# Revit family: WALL SQUARE 6W SIMETRICA_LKB0635A_WW
name_source: partatom
category: Luminarias
units: mm (PartAtom-declared; Revit-internal decimal feet)

## family parameters
Compartido = No
Corte con vacíos al cargar = No
Cota de conector redondo = Diámetro de uso
Origen de luz = Sí
Punto de cálculo de habitación = No
Se basa en plano de trabajo = Sí
Siempre vertical = No
Tipo de pieza = Normal

## types (8) — shared parameters
Ancho = 160 mm  [stored 0.524934 ft]
Cambio de temperatura de color de luz atenuada = <Ninguno>
Comentarios de vataje = 100-240V
Fabricante = BRILLANT
Filtro de color = 16777215
Longitud de símbolo de origen de luz = 500 mm  [stored 1.64042 ft]
Lámpara = OSRAM
Watt per fixture = 6
Ángulo de inclinación = 105.00°
zero-valued in all types: Elevación por defecto

## per-type parameters (varying)
| type | Descripción | Modelo | Ángulo de campo de foco | Ángulo de enfoque |
| EMP_LKB0635A.30 | LUMINARIA TIPO CUADRADO PARA EMPOTRAR EN PISO CON CUERPO DE ALUMINIO FUNDIDO A PRESION, CUBIERTO CON POLVO GRIS OSCURO CON CUBIERTA DE ACERO INOXIDABLE Y VIDRIO TEMPLADO DE 8MM, HOUSING DE METAL 1.5MM CUBIERTO DE POLVO GRIS OSCURO DE 160MM Y 118MM DE PROFUNDO CON PESO DE 2.5KG. CUENTA CON 6 LED TIPO OSRAM CON UNA POTENCIA TOTAL DE 6W, TEMPERATURA EN BLANCO ULTRA CALIDO EN 2000K CON 269 LUMENES, IP67, IK09, IRC 80 APERTURA EN 30 GRADOS POR STOCK, ALIMENTADA A 100-240V. | LKB0635A.30 | 30.00° | 30.00° |
| EMP_LKB0635A.6 | LUMINARIA TIPO CUADRADO PARA EMPOTRAR EN PISO CON CUERPO DE ALUMINIO FUNDIDO A PRESION, CUBIERTO CON POLVO GRIS OSCURO CON CUBIERTA DE ACERO INOXIDABLE Y VIDRIO TEMPLADO DE 8MM, HOUSING DE METAL 1.5MM CUBIERTO DE POLVO GRIS OSCURO DE 160MM Y 118MM DE PROFUNDO CON PESO DE 2.5KG. CUENTA CON 6 LED TIPO OSRAM CON UNA POTENCIA TOTAL DE 6W, TEMPERATURA EN BLANCO ULTRA CALIDO EN 2000K CON 269 LUMENES, IP67, IK09, IRC 80 APERTURA EN 6 GRADOS POR PROYECTO, ALIMENTADA A 100-240V. | LKB0635A.6 | 6.00° | 6.00° |
| EMP_LKB0635A.13 | LUMINARIA TIPO CUADRADO PARA EMPOTRAR EN PISO CON CUERPO DE ALUMINIO FUNDIDO A PRESION, CUBIERTO CON POLVO GRIS OSCURO CON CUBIERTA DE ACERO INOXIDABLE Y VIDRIO TEMPLADO DE 8MM, HOUSING DE METAL 1.5MM CUBIERTO DE POLVO GRIS OSCURO DE 160MM Y 118MM DE PROFUNDO CON PESO DE 2.5KG. CUENTA CON 6 LED TIPO OSRAM CON UNA POTENCIA TOTAL DE 6W, TEMPERATURA EN BLANCO ULTRA CALIDO EN 2000K CON 269 LUMENES, IP67, IK09, IRC 80 APERTURA EN 13 GRADOS POR PROYECTO, ALIMENTADA A 100-240V. | LKB0635A.13 | 13.00° | 13.00° |
| EMP_LKB0635A.20 | LUMINARIA TIPO CUADRADO PARA EMPOTRAR EN PISO CON CUERPO DE ALUMINIO FUNDIDO A PRESION, CUBIERTO CON POLVO GRIS OSCURO CON CUBIERTA DE ACERO INOXIDABLE Y VIDRIO TEMPLADO DE 8MM, HOUSING DE METAL 1.5MM CUBIERTO DE POLVO GRIS OSCURO DE 160MM Y 118MM DE PROFUNDO CON PESO DE 2.5KG. CUENTA CON 6 LED TIPO OSRAM CON UNA POTENCIA TOTAL DE 6W, TEMPERATURA EN BLANCO ULTRA CALIDO EN 2000K CON 269 LUMENES, IP67, IK09, IRC 80 APERTURA EN 20 GRADOS POR PROYECTO, ALIMENTADA A 100-240V. | LKB0635A.20 | 20.00° | 20.00° |
| EMP_LKB0635WW.30 | LUMINARIA TIPO CUADRADO PARA EMPOTRAR EN PISO CON CUERPO DE ALUMINIO FUNDIDO A PRESION, CUBIERTO CON POLVO GRIS OSCURO CON CUBIERTA DE ACERO INOXIDABLE Y VIDRIO TEMPLADO DE 8MM, HOUSING DE METAL 1.5MM CUBIERTO DE POLVO GRIS OSCURO DE 160MM Y 118MM DE PROFUNDO CON PESO DE 2.5KG. CUENTA CON 6 LED TIPO OSRAM CON UNA POTENCIA TOTAL DE 6W, TEMPERATURA EN BLANCO CALIDO EN 3000K CON 269 LUMENES, IP67, IK09, IRC 80 APERTURA EN 30 GRADOS POR STOCK, ALIMENTADA A 100-240V. | LKB0635WW.30 | 30.00° | 30.00° |
| EMP_LKB0635WW.6 | LUMINARIA TIPO CUADRADO PARA EMPOTRAR EN PISO CON CUERPO DE ALUMINIO FUNDIDO A PRESION, CUBIERTO CON POLVO GRIS OSCURO CON CUBIERTA DE ACERO INOXIDABLE Y VIDRIO TEMPLADO DE 8MM, HOUSING DE METAL 1.5MM CUBIERTO DE POLVO GRIS OSCURO DE 160MM Y 118MM DE PROFUNDO CON PESO DE 2.5KG. CUENTA CON 6 LED TIPO OSRAM CON UNA POTENCIA TOTAL DE 6W, TEMPERATURA EN BLANCO CALIDO EN 3000K CON 269 LUMENES, IP67, IK09, IRC 80 APERTURA EN 6 GRADOS POR PROYECTO, ALIMENTADA A 100-240V. | LKB0635WW.6 | 6.00° | 6.00° |
| EMP_LKB0635WW.13 | LUMINARIA TIPO CUADRADO PARA EMPOTRAR EN PISO CON CUERPO DE ALUMINIO FUNDIDO A PRESION, CUBIERTO CON POLVO GRIS OSCURO CON CUBIERTA DE ACERO INOXIDABLE Y VIDRIO TEMPLADO DE 8MM, HOUSING DE METAL 1.5MM CUBIERTO DE POLVO GRIS OSCURO DE 160MM Y 118MM DE PROFUNDO CON PESO DE 2.5KG. CUENTA CON 6 LED TIPO OSRAM CON UNA POTENCIA TOTAL DE 6W, TEMPERATURA EN BLANCO CALIDO EN 3000K CON 269 LUMENES, IP67, IK09, IRC 80 APERTURA EN 13 GRADOS POR PROYECTO, ALIMENTADA A 100-240V. | LKB0635WW.13 | 13.00° | 13.00° |
| EMP_LKB0635WW.20 | LUMINARIA TIPO CUADRADO PARA EMPOTRAR EN PISO CON CUERPO DE ALUMINIO FUNDIDO A PRESION, CUBIERTO CON POLVO GRIS OSCURO CON CUBIERTA DE ACERO INOXIDABLE Y VIDRIO TEMPLADO DE 8MM, HOUSING DE METAL 1.5MM CUBIERTO DE POLVO GRIS OSCURO DE 160MM Y 118MM DE PROFUNDO CON PESO DE 2.5KG. CUENTA CON 6 LED TIPO OSRAM CON UNA POTENCIA TOTAL DE 6W, TEMPERATURA EN BLANCO CALIDO EN 3000K CON 269 LUMENES, IP67, IK09, IRC 80 APERTURA EN 20 GRADOS POR PROYECTO, ALIMENTADA A 100-240V. | LKB0635WW.20 | 20.00° | 20.00° |

note: [stored X ft] marks values corroborated as IEEE doubles in the binary element streams (Revit-internal decimal feet)

## geometry (parser evidence)
native form markers: Blend x2
no freeform markers — native parametric forms only
